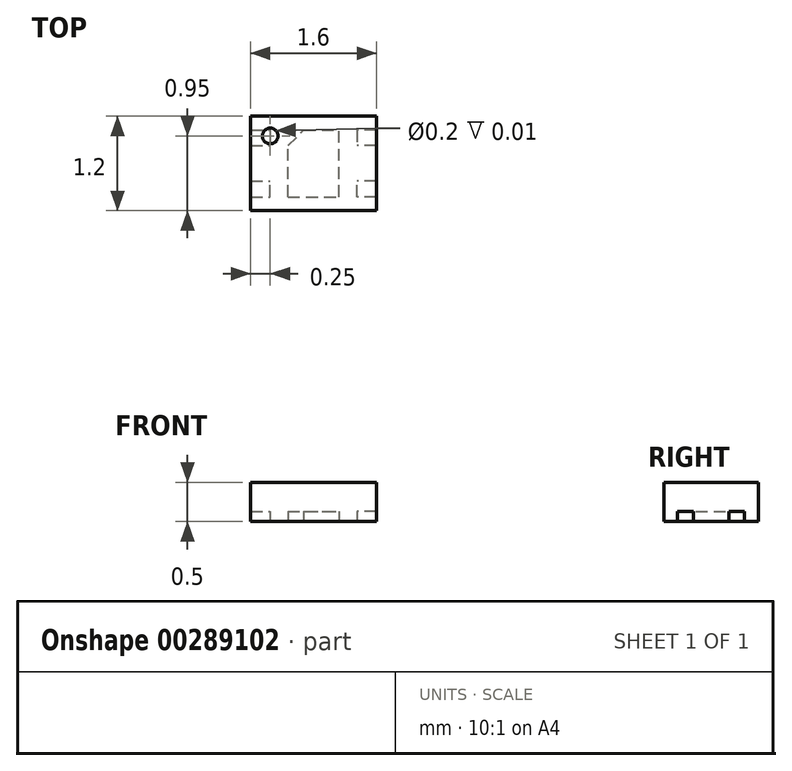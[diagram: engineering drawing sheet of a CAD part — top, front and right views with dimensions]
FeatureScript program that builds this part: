
annotation { "Feature Type Name" : "Feature", "Feature Type Description" : "" }
export const myFeature = defineFeature(function(context is Context, id is Id, definition is map)
    precondition{}
    {
        {
            var Q0;
            Q0=qCreatedBy(makeId("Top.planeOp"),FACE);
            var sketch = newSketch(context, id + "F0", { "sketchPlane" : qUnion([Q0])});
            skLineSegment(sketch, "E0.bottom", {"start": v(-0.8, 0.6) * mm, "end": v(0.8, 0.6) * mm});
            skLineSegment(sketch, "E0.top", {"start": v(-0.8, -0.6) * mm, "end": v(0.8, -0.6) * mm});
            skLineSegment(sketch, "E0.left", {"start": v(-0.8, 0.6) * mm, "end": v(-0.8, -0.6) * mm});
            skLineSegment(sketch, "E0.right", {"start": v(0.8, 0.6) * mm, "end": v(0.8, -0.6) * mm});
            skPoint(sketch, "E0.middle", {"position": v(0, 0) * mm});
            skSolve(sketch);
        }
        {
            var Q0;
            Q0 = qSketchRegion(id + "F0", true);
            extrude(context, id + "F1", {"entities" : qUnion([Q0]), "flatOperationType" : FlatOperationType.REMOVE, "offsetDistance" : 25 * mm, "depth" : 0.5 * mm, "domain" : OperationDomain.MODEL});
        }
        {
            var Q0;
            Q0=makeQuery(id+"F1.opExtrude","CAP_FACE",FACE,{"disambiguationData":[OSD([sQuery(id+"F0.wireOp",EDGE,"E0.bottom"),sQuery(id+"F0.wireOp",EDGE,"E0.top"),sQuery(id+"F0.wireOp",EDGE,"E0.left"),sQuery(id+"F0.wireOp",EDGE,"E0.right")])],"isStart":true});
            var sketch = newSketch(context, id + "F2", { "sketchPlane" : qUnion([Q0])});
            skLineSegment(sketch, "E1.bottom", {"start": v(-0.8, 0.43) * mm, "end": v(-0.55, 0.43) * mm});
            skLineSegment(sketch, "E1.top", {"start": v(-0.8, 0.23) * mm, "end": v(-0.55, 0.23) * mm});
            skLineSegment(sketch, "E1.left", {"start": v(-0.8, 0.42) * mm, "end": v(-0.8, 0.23) * mm});
            skLineSegment(sketch, "E1.right", {"start": v(-0.55, 0.43) * mm, "end": v(-0.55, 0.23) * mm});
            skPoint(sketch, "E2", {"position": v(-0.8, 0.33) * mm});
            skLineSegment(sketch, "E3.MirrorCS", {"start": v(-0.8, -0.23) * mm, "end": v(-0.55, -0.23) * mm});
            skLineSegment(sketch, "E4.MirrorCS", {"start": v(-0.8, -0.42) * mm, "end": v(-0.8, -0.23) * mm});
            skLineSegment(sketch, "E5.MirrorCS", {"start": v(-0.8, -0.43) * mm, "end": v(-0.55, -0.43) * mm});
            skLineSegment(sketch, "E6.MirrorCS", {"start": v(-0.55, -0.43) * mm, "end": v(-0.55, -0.23) * mm});
            skLineSegment(sketch, "E7", {"start": v(0, 0.6) * mm, "end": v(0, 0) * mm, "construction": true});
            skLineSegment(sketch, "E8.MirrorCS", {"start": v(0.8, 0.43) * mm, "end": v(0.8, 0.23) * mm});
            skLineSegment(sketch, "E9.MirrorCS", {"start": v(0.8, 0.43) * mm, "end": v(0.55, 0.43) * mm});
            skLineSegment(sketch, "E10.MirrorCS", {"start": v(0.8, 0.23) * mm, "end": v(0.55, 0.23) * mm});
            skLineSegment(sketch, "E11.MirrorCS", {"start": v(0.55, 0.43) * mm, "end": v(0.55, 0.23) * mm});
            skLineSegment(sketch, "E12.MirrorCS", {"start": v(0.8, -0.22) * mm, "end": v(0.55, -0.22) * mm});
            skLineSegment(sketch, "E13.MirrorCS", {"start": v(0.8, -0.42) * mm, "end": v(0.8, -0.22) * mm});
            skPoint(sketch, "E14.MirrorP", {"position": v(0.8, 0.33) * mm});
            skLineSegment(sketch, "E15.MirrorCS", {"start": v(0.8, -0.42) * mm, "end": v(0.55, -0.42) * mm});
            skLineSegment(sketch, "E16.MirrorCS", {"start": v(0.55, -0.42) * mm, "end": v(0.55, -0.22) * mm});
            skLineSegment(sketch, "E17.bottom", {"start": v(-0.33, 0.42) * mm, "end": v(0.33, 0.42) * mm});
            skLineSegment(sketch, "E17.top", {"start": v(-0.13, -0.42) * mm, "end": v(0.32, -0.42) * mm});
            skLineSegment(sketch, "E17.left", {"start": v(-0.33, 0.42) * mm, "end": v(-0.33, -0.23) * mm});
            skLineSegment(sketch, "E17.right", {"start": v(0.33, 0.42) * mm, "end": v(0.32, -0.42) * mm});
            skPoint(sketch, "E17.middle", {"position": v(0, 0) * mm});
            skPoint(sketch, "E18", {"position": v(-0.33, -0.22) * mm});
            skPoint(sketch, "E19", {"position": v(-0.13, -0.42) * mm});
            skLineSegment(sketch, "E20", {"start": v(-0.33, -0.22) * mm, "end": v(-0.12, -0.43) * mm});
            skPoint(sketch, "E21.orphan", {"position": v(-0.33, -0.42) * mm});
            skSolve(sketch);
        }
        {
            var Q0;
            Q0 = qSketchRegion(id + "F2", true);
            extrude(context, id + "F3", {"entities" : qUnion([Q0]), "flatOperationType" : FlatOperationType.REMOVE, "oppositeDirection" : true, "offsetDistance" : 25 * mm, "depth" : 0.13 * mm, "domain" : OperationDomain.MODEL});
        }
        {
            var Q0;
            Q0=makeQuery(id+"F3.opExtrude","SWEPT_BODY",BODY,{"disambiguationData":[OSD([sQuery(id+"F2.wireOp",EDGE,"E1.bottom"),sQuery(id+"F2.wireOp",EDGE,"E1.top"),sQuery(id+"F2.wireOp",EDGE,"E1.left"),sQuery(id+"F2.wireOp",EDGE,"E1.right")])]});
            var Q1;
            Q1=makeQuery(id+"F3.opExtrude","SWEPT_BODY",BODY,{"disambiguationData":[OSD([sQuery(id+"F2.wireOp",EDGE,"E3.MirrorCS"),sQuery(id+"F2.wireOp",EDGE,"E4.MirrorCS"),sQuery(id+"F2.wireOp",EDGE,"E5.MirrorCS"),sQuery(id+"F2.wireOp",EDGE,"E6.MirrorCS")])]});
            var Q2;
            Q2=makeQuery(id+"F3.opExtrude","SWEPT_BODY",BODY,{"disambiguationData":[OSD([sQuery(id+"F2.wireOp",EDGE,"E8.MirrorCS"),sQuery(id+"F2.wireOp",EDGE,"E9.MirrorCS"),sQuery(id+"F2.wireOp",EDGE,"E10.MirrorCS"),sQuery(id+"F2.wireOp",EDGE,"E11.MirrorCS")])]});
            var Q3;
            Q3=makeQuery(id+"F3.opExtrude","SWEPT_BODY",BODY,{"disambiguationData":[OSD([sQuery(id+"F2.wireOp",EDGE,"E12.MirrorCS"),sQuery(id+"F2.wireOp",EDGE,"E13.MirrorCS"),sQuery(id+"F2.wireOp",EDGE,"E15.MirrorCS"),sQuery(id+"F2.wireOp",EDGE,"E16.MirrorCS")])]});
            var Q4;
            Q4=makeQuery(id+"F3.opExtrude","SWEPT_BODY",BODY,{"disambiguationData":[OSD([sQuery(id+"F2.wireOp",EDGE,"E17.bottom"),sQuery(id+"F2.wireOp",EDGE,"E17.top"),sQuery(id+"F2.wireOp",EDGE,"E17.left"),sQuery(id+"F2.wireOp",EDGE,"E17.right"),sQuery(id+"F2.wireOp",EDGE,"E20")])]});
            var Q5;
            Q5=makeQuery(id+"F1.opExtrude","SWEPT_BODY",BODY,{"disambiguationData":[OSD([sQuery(id+"F0.wireOp",EDGE,"E0.bottom"),sQuery(id+"F0.wireOp",EDGE,"E0.top"),sQuery(id+"F0.wireOp",EDGE,"E0.left"),sQuery(id+"F0.wireOp",EDGE,"E0.right")])]});
            booleanBodies(context, id + "F4", {"operationType" : BooleanOperationType.SUBTRACTION, "tools" : qUnion([Q0, Q1, Q2, Q3, Q4]), "targets" : qUnion([Q5]), "keepTools" : true});
        }
        {
            var Q0;
            Q0=makeQuery(id+"F1.opExtrude","CAP_FACE",FACE,{"disambiguationData":[OSD([sQuery(id+"F0.wireOp",EDGE,"E0.bottom"),sQuery(id+"F0.wireOp",EDGE,"E0.top"),sQuery(id+"F0.wireOp",EDGE,"E0.left"),sQuery(id+"F0.wireOp",EDGE,"E0.right")])],"isStart":false});
            var sketch = newSketch(context, id + "F5", { "sketchPlane" : qUnion([Q0])});
            skCircle(sketch, "E22", {"center": v(-0.55, 0.35) * mm, "radius": 0.1 * mm});
            skSolve(sketch);
        }
        {
            var Q0;
            Q0 = qSketchRegion(id + "F5", true);
            extrude(context, id + "F6", {"entities" : qUnion([Q0]), "flatOperationType" : FlatOperationType.REMOVE, "oppositeDirection" : true, "offsetDistance" : 25 * mm, "depth" : 0.01 * mm, "domain" : OperationDomain.MODEL});
        }
        {
            var Q0;
            Q0=makeQuery(id+"F6.opExtrude","SWEPT_BODY",BODY,{"disambiguationData":[OSD([sQuery(id+"F5.wireOp",EDGE,"E22")])]});
            var Q1;
            Q1=makeQuery(id+"F1.opExtrude","SWEPT_BODY",BODY,{"disambiguationData":[OSD([sQuery(id+"F0.wireOp",EDGE,"E0.bottom"),sQuery(id+"F0.wireOp",EDGE,"E0.top"),sQuery(id+"F0.wireOp",EDGE,"E0.left"),sQuery(id+"F0.wireOp",EDGE,"E0.right")])]});
            booleanBodies(context, id + "F7", {"operationType" : BooleanOperationType.SUBTRACTION, "tools" : qUnion([Q0]), "targets" : qUnion([Q1]), "keepTools" : true});
        }
    });
